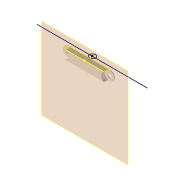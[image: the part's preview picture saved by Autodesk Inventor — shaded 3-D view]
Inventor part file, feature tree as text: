
AUTODESK INVENTOR PART (.ipt)
format: ipt  version: 2022 (Build 260153000, 153)  size: 112,640 bytes
history: native  units: mm
features: sketch x3, reference x3, projected_geometry x2, other x2, plane x1, extrude x1, hole x1
ambient origin geometry x8: Origin, YZ Plane, XZ Plane, XY Plane, X Axis, Y Axis, Z Axis, Center Point
bodies: Volumenkörper1 (feature_tree)
feature tree (13):
  plane  "Arbeitsebene1"
  extrude  "Extrusion1"  Depth=4.0mm TaperAngle=0.0deg
  hole  "Bohrung1"  [1 undecoded]
  sketch  "Skizze3"
  sketch  "Skizze1"  dims[d0=6.0mm d1=4.0mm d2=0.0mm]
  reference  "Referenz1"
  reference  "Referenz2"
  reference  "Referenz3"
  sketch  "Skizze2"  dims[d3=2.8mm d4=6.0mm d5=6.5mm d6=2.5mm d7=90.0deg d8=7.0mm d9=20.594885mm]
  projected_geometry  "Projizierte Kontur1"
  projected_geometry  "Projizierte Kontur2"
  other  "Assembly_USB_Lampassembly.iam"
  other  "Matchboxscope_layer_ikealamp:1"
note: 1 required parameter value undecoded (feature->parameter linkage not recoverable at this tier; creation-order binding heuristic only, values carry confidence <= 0.55)
